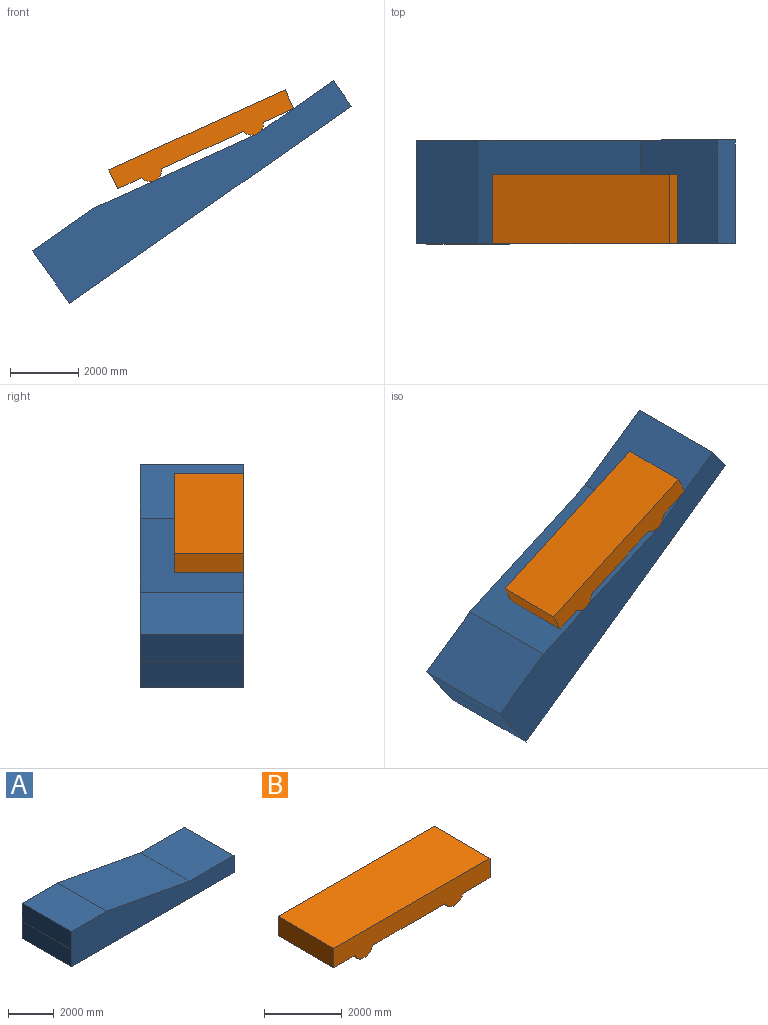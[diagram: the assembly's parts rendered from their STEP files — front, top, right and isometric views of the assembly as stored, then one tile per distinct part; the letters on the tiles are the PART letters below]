
ASSEMBLY  parts=2 mates=1
PART A: 9 faces, bbox 10106.4x3048x1882.9 mm
  f0: plane 3048x2743.2mm, normal (0,0,1), area 8361273.6mm2, adj f1,f6,f7,f8
  f1: plane 5168.45x3048mm, normal (0.18,0,0.98), area 16025774.4mm2, adj f0,f2,f7,f8
  f2: plane 3048x2194.75mm, normal (0,0,1), area 6689585.8mm2, adj f1,f3,f7,f8
  f3: plane 3048x965.2mm, normal (-1,0,0), area 2941929.6mm2, adj f2,f4,f7,f8
  f4: plane 3048x917.72mm, normal (-1,0,0), area 2797213.3mm2, adj f3,f5,f7,f8
  f5: plane 10103.44x3048mm, normal (0,0,-1), area 30795276.3mm2, adj f4,f6,f7,f8
  f6: plane 3048x917.72mm, normal (1,0,0), area 2797198.8mm2, adj f0,f5,f7,f8
  f7: plane 10106.39x1882.92mm, normal (0,-1,0), area 13886105.5mm2, adj f0,f1,f2,f3,f4,f5,f6
  f8: plane 10106.39x1882.92mm, normal (0,1,0), area 13886105.5mm2, adj f0,f1,f2,f3,f4,f5,f6
PART B: 10 faces, bbox 5689.6x2032x840.2 mm
  f0: cylinder r=342.9mm len=2032mm, axis (0,-1,0), area 1723816.9mm2, adj f1,f7,f8,f9
  f1: plane 2641.35x2032mm, normal (0,0,-1), area 5367227.9mm2, adj f0,f2,f8,f9
  f2: cylinder r=342.9mm len=2032mm, axis (0,-1,0), area 1723816.9mm2, adj f1,f3,f8,f9
  f3: plane 2032x979.29mm, normal (0,0,-1), area 1989923.2mm2, adj f2,f4,f8,f9
  f4: plane 2032x609.6mm, normal (1,0,0), area 1238707.2mm2, adj f3,f5,f8,f9
  f5: plane 5689.6x2032mm, normal (0,0,1), area 11561267.2mm2, adj f4,f6,f8,f9
  f6: plane 2032x609.6mm, normal (-1,0,0), area 1238707.2mm2, adj f5,f7,f8,f9
  f7: plane 2032x773.06mm, normal (0,0,-1), area 1570856.7mm2, adj f0,f6,f8,f9
  f8: plane 5689.6x840.16mm, normal (0,1,0), area 3686480.7mm2, adj f0,f1,f2,f3,f4,f5,f6,f7
  f9: plane 5689.6x840.16mm, normal (0,-1,0), area 3686480.7mm2, adj f0,f1,f2,f3,f4,f5,f6,f7
PLACE A rot(axis=(0,-1,0),35deg) t=(1027.9,1148.33,2450.82)mm fixed
PLACE B rot(axis=(0,-1,0),24.5deg) t=(4039.68,1148.33,884.98)mm
MATE planar A.f7 <-> B.f0  axis (0,-1,0) through (-1424.99,-1899.67,519.64)mm
